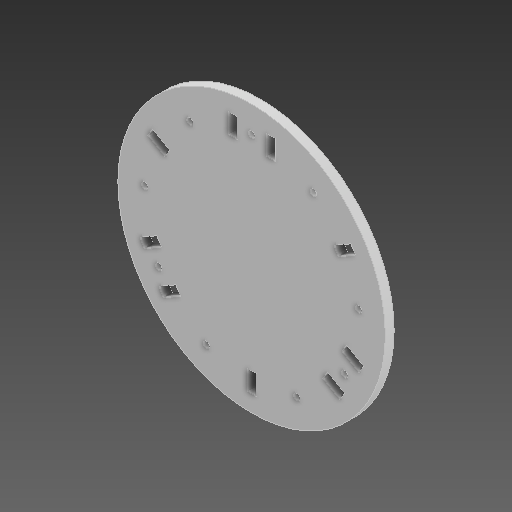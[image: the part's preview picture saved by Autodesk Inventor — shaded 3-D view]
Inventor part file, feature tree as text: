
AUTODESK INVENTOR PART (.ipt)
format: ipt  version: 2020.1 (Build 241239000, 239)  size: 160,256 bytes
history: native  units: mm
features: other x6, sketch x1
ambient origin geometry x8: Origin, YZ Plane, XZ Plane, XY Plane, X Axis, Y Axis, Z Axis, Center Point
bodies: Solid1 (feature_tree)
feature tree (7):
  other  "Prototype Plate Base.ipt"
  other  "Solid1::Prototype Plate Base.ipt"
  other  "TaggingFeature1"
  sketch  "Sketch the Prototype Plate Base Profile"  dims[d0=10.0mm]
  other  "Locate the Outer Rib Slots"
  other  "Locate the Inner Rib Slot"
  other  "Locate Holes for Connecting Two Bases"
